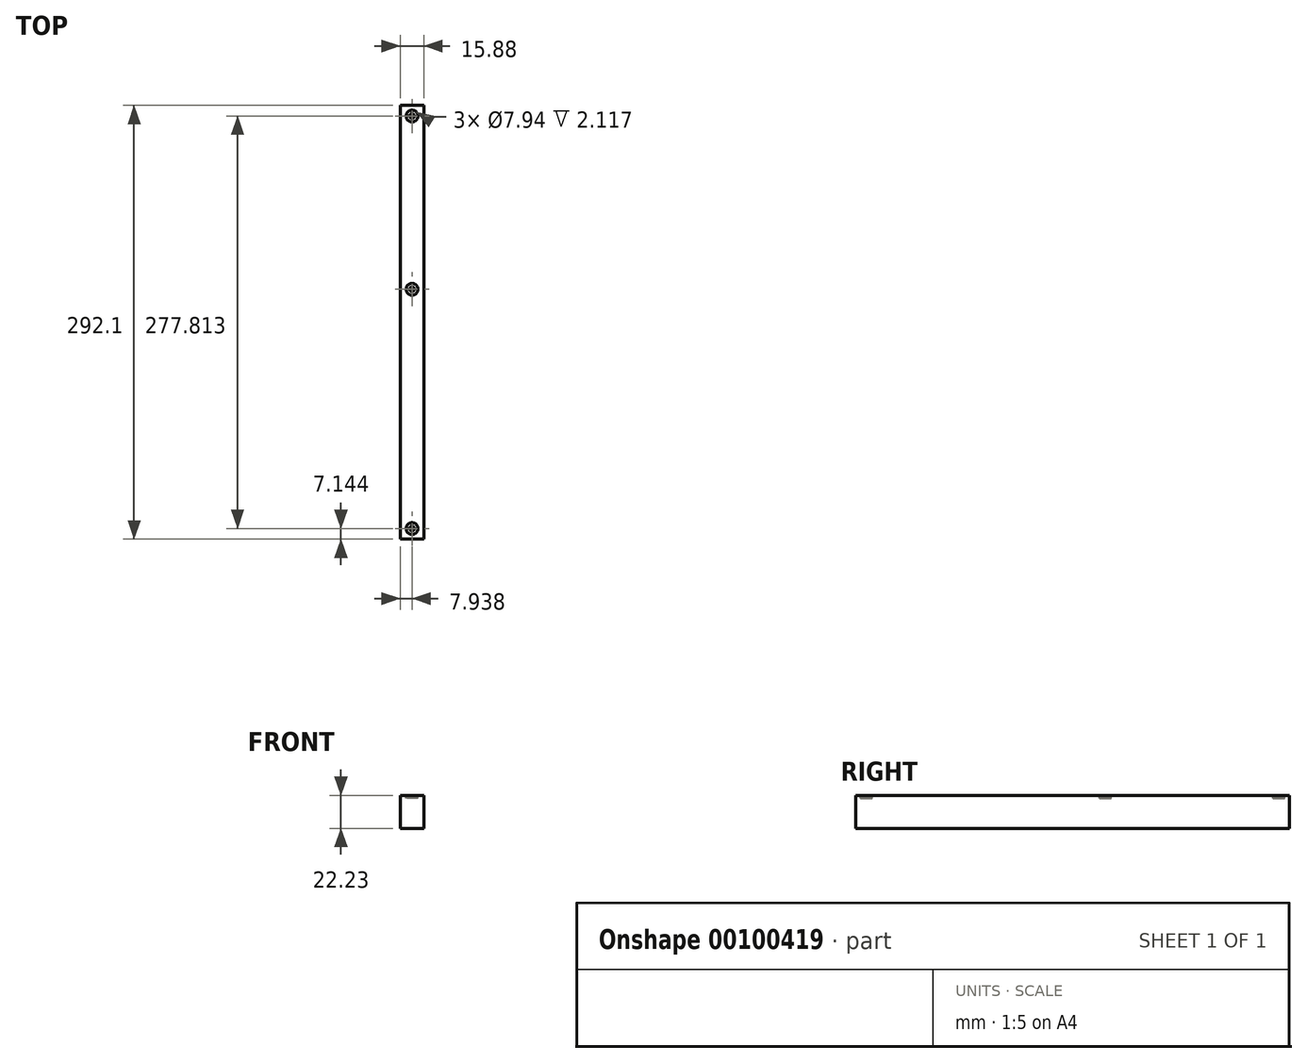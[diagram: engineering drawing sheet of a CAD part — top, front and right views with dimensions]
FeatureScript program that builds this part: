
annotation { "Feature Type Name" : "Feature", "Feature Type Description" : "" }
export const myFeature = defineFeature(function(context is Context, id is Id, definition is map)
    precondition{}
    {
        {
            var Q0;
            Q0=qCreatedBy(makeId("Front.planeOp"),FACE);
            var sketch = newSketch(context, id + "F0", { "sketchPlane" : qUnion([Q0])});
            skLineSegment(sketch, "E0.bottom", {"start": v(0, 0) * mm, "end": v(15.88, 0) * mm});
            skLineSegment(sketch, "E0.top", {"start": v(0, 22.23) * mm, "end": v(15.87, 22.23) * mm});
            skLineSegment(sketch, "E0.left", {"start": v(0, 0) * mm, "end": v(0, 22.23) * mm});
            skLineSegment(sketch, "E0.right", {"start": v(15.88, 0) * mm, "end": v(15.87, 22.23) * mm});
            skSolve(sketch);
        }
        {
            var Q0;
            Q0 = qSketchRegion(id + "F0", true);
            extrude(context, id + "F1", {"entities" : qUnion([Q0]), "oppositeDirection" : true, "depth" : 292.1 * mm});
        }
        {
            var Q0;
            Q0=makeQuery(id+"F1.opExtrude","SWEPT_FACE",FACE,{"disambiguationData":[OSD([sQuery(id+"F0.wireOp",EDGE,"E0.top")])]});
            var sketch = newSketch(context, id + "F2", { "sketchPlane" : qUnion([Q0])});
            skCircle(sketch, "E1", {"center": v(7.94, 7.14) * mm, "radius": 3.97 * mm});
            skLineSegment(sketch, "E2", {"start": v(7.94, 7.14) * mm, "end": v(15.88, 7.14) * mm});
            skLineSegment(sketch, "E3", {"start": v(7.94, 7.14) * mm, "end": v(0, 7.14) * mm});
            skCircle(sketch, "E4", {"center": v(7.94, 7.14) * mm, "radius": 1.59 * mm});
            skLineSegment(sketch, "E5", {"start": v(7.94, 5.56) * mm, "end": v(7.94, 0) * mm});
            skCircle(sketch, "E6", {"center": v(7.94, 284.96) * mm, "radius": 3.97 * mm});
            skPoint(sketch, "E6.centerSnap0", {"position": v(7.94, 292.1) * mm});
            skCircle(sketch, "E7", {"center": v(7.94, 284.96) * mm, "radius": 1.59 * mm});
            skLineSegment(sketch, "E8", {"start": v(7.94, 283.37) * mm, "end": v(7.94, 169.86) * mm});
            skCircle(sketch, "E9", {"center": v(7.94, 168.28) * mm, "radius": 1.59 * mm});
            skLineSegment(sketch, "E10", {"start": v(7.94, 168.28) * mm, "end": v(7.94, 169.86) * mm});
            skCircle(sketch, "E11", {"center": v(7.94, 168.28) * mm, "radius": 3.97 * mm});
            skSolve(sketch);
        }
        {
            var Q0;
            Q0=makeQuery(id+"F2.imprint","IMPRINT",FACE,{"disambiguationData":[TD([[makeQuery(id+"F2.imprint","IMPRINT",EDGE,{"derivedFrom":sQuery(id+"F2.wireOp",EDGE,"E6")}),1.0]])]});
            var Q1;
            Q1=makeQuery(id+"F2.imprint","IMPRINT",FACE,{"disambiguationData":[TD([[makeQuery(id+"F2.imprint","IMPRINT",EDGE,{"derivedFrom":sQuery(id+"F2.wireOp",EDGE,"E9")}),-1.0]])]});
            var Q2;
            {var subQ0=sQuery(id+"F2.wireOp",EDGE,"E3");var subQ1=sQuery(id+"F2.wireOp",EDGE,"E1");var subQ2=makeQuery(id+"F2.imprint","INTERSECT",VERTEX,{"derivedFrom":[subQ1,subQ0]});Q2=makeQuery(id+"F2.imprint","IMPRINT",FACE,{"disambiguationData":[TD([[makeQuery(id+"F2.imprint","IMPRINT",EDGE,{"disambiguationData":[TD([[subQ2,1.0]])],"derivedFrom":subQ1}),1.0]])]});}
            var Q3;
            {var subQ0=sQuery(id+"F2.wireOp",EDGE,"E3");var subQ1=sQuery(id+"F2.wireOp",EDGE,"E1");var subQ2=makeQuery(id+"F2.imprint","INTERSECT",VERTEX,{"derivedFrom":[subQ1,subQ0]});Q3=makeQuery(id+"F2.imprint","IMPRINT",FACE,{"disambiguationData":[TD([[makeQuery(id+"F2.imprint","IMPRINT",EDGE,{"disambiguationData":[TD([[subQ2,-1.0]])],"derivedFrom":subQ1}),1.0]])]});}
            var Q4;
            {var subQ0=sQuery(id+"F2.wireOp",EDGE,"E2");var subQ1=sQuery(id+"F2.wireOp",EDGE,"E1");var subQ2=makeQuery(id+"F2.imprint","INTERSECT",VERTEX,{"derivedFrom":[subQ1,subQ0]});Q4=makeQuery(id+"F2.imprint","IMPRINT",FACE,{"disambiguationData":[TD([[makeQuery(id+"F2.imprint","IMPRINT",EDGE,{"disambiguationData":[TD([[subQ2,1.0]])],"derivedFrom":subQ1}),1.0]])]});}
            extrude(context, id + "F3", {"entities" : qUnion([Q0, Q1, Q2, Q3, Q4]), "operationType" : NewBodyOperationType.REMOVE, "oppositeDirection" : true, "depth" : 2.12 * mm});
        }
    });
